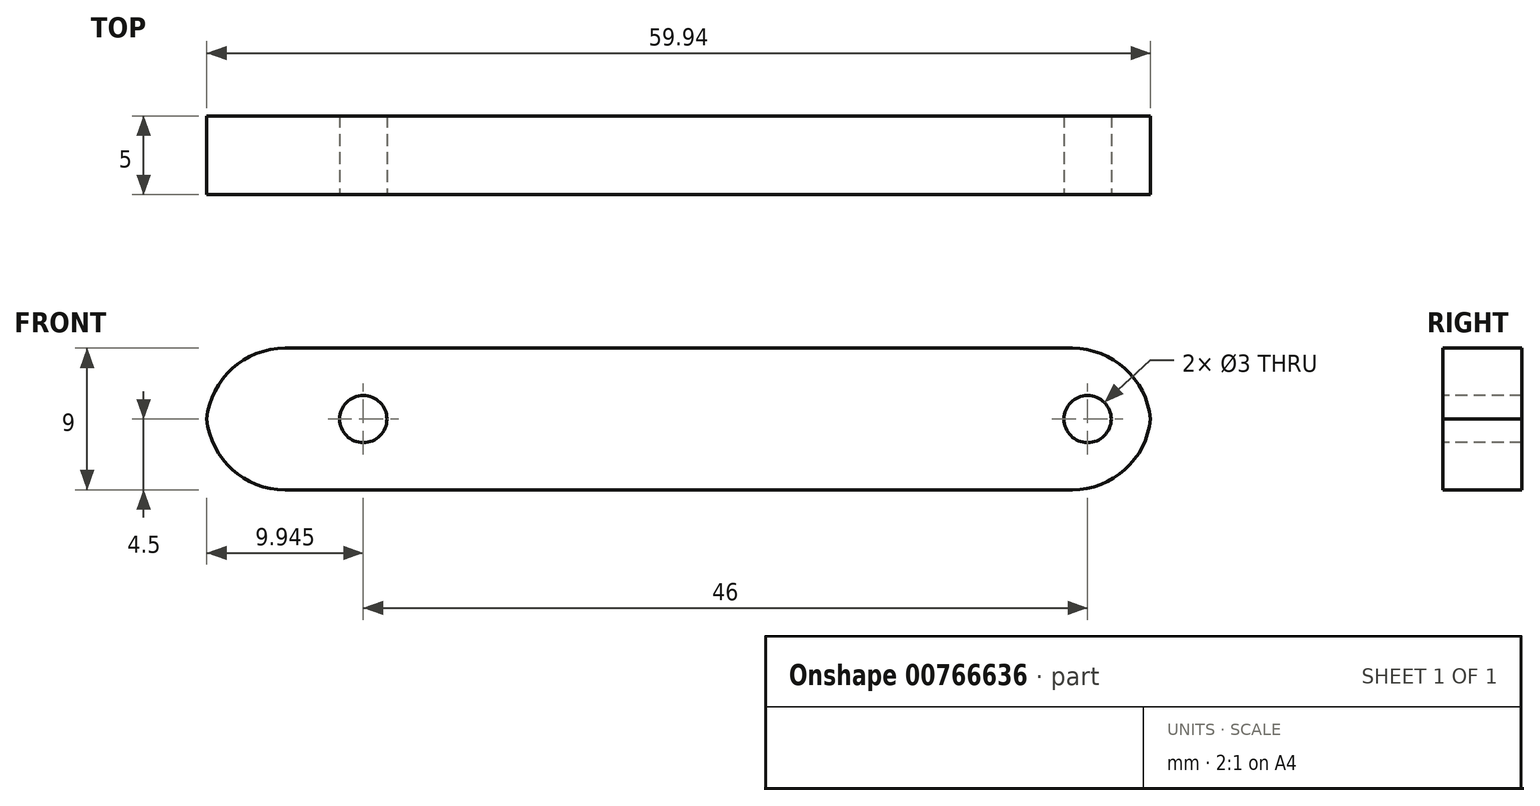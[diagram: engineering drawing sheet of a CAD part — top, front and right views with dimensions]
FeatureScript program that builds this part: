
annotation { "Feature Type Name" : "Feature", "Feature Type Description" : "" }
export const myFeature = defineFeature(function(context is Context, id is Id, definition is map)
    precondition{}
    {
        {
            var Q0;
            Q0=qCreatedBy(makeId("Front.planeOp"),FACE);
            var sketch = newSketch(context, id + "F0", { "sketchPlane" : qUnion([Q0])});
            skLineSegment(sketch, "E0.bottom", {"start": v(-30, 4.5) * mm, "end": v(30, 4.5) * mm});
            skLineSegment(sketch, "E0.top", {"start": v(-30, -4.5) * mm, "end": v(30, -4.5) * mm});
            skLineSegment(sketch, "E0.left", {"start": v(-30, 4.5) * mm, "end": v(-30, -4.5) * mm});
            skLineSegment(sketch, "E0.right", {"start": v(30, 4.5) * mm, "end": v(30, -4.5) * mm});
            skPoint(sketch, "E0.middle", {"position": v(0, 0) * mm});
            skSolve(sketch);
        }
        {
            var Q0;
            Q0=makeQuery(id+"F0.imprint","IMPRINT",FACE,{"disambiguationData":[TD([[makeQuery(id+"F0.imprint","IMPRINT",EDGE,{"derivedFrom":sQuery(id+"F0.wireOp",EDGE,"E0.bottom")}),-1.0]])]});
            extrude(context, id + "F1", {"entities" : qUnion([Q0]), "depth" : 5 * mm, "offsetDistance" : 25 * mm});
        }
        {
            var Q0;
            Q0=makeQuery(id+"F1.opExtrude","SWEPT_EDGE",EDGE,{"disambiguationData":[OSD([sQuery(id+"F0.wireOp",EDGE,"E0.bottom"),sQuery(id+"F0.wireOp",EDGE,"E0.left")])]});
            var Q1;
            Q1=makeQuery(id+"F1.opExtrude","SWEPT_EDGE",EDGE,{"disambiguationData":[OSD([sQuery(id+"F0.wireOp",EDGE,"E0.top"),sQuery(id+"F0.wireOp",EDGE,"E0.left")])]});
            var Q2;
            Q2=makeQuery(id+"F1.opExtrude","SWEPT_EDGE",EDGE,{"disambiguationData":[OSD([sQuery(id+"F0.wireOp",EDGE,"E0.bottom"),sQuery(id+"F0.wireOp",EDGE,"E0.right")])]});
            var Q3;
            Q3=makeQuery(id+"F1.opExtrude","SWEPT_EDGE",EDGE,{"disambiguationData":[OSD([sQuery(id+"F0.wireOp",EDGE,"E0.top"),sQuery(id+"F0.wireOp",EDGE,"E0.right")])]});
            fillet(context, id + "F2", {"entities" : qUnion([Q0, Q1, Q2, Q3]), "radius" : 5 * mm, "tangentPropagation" : true, "allowEdgeOverflow" : false});
        }
        {
            var Q0;
            Q0=qCreatedBy(makeId("Front.planeOp"),FACE);
            var sketch = newSketch(context, id + "F3", { "sketchPlane" : qUnion([Q0])});
            skCircle(sketch, "E1", {"center": v(25.97, 0) * mm, "radius": 1.5 * mm});
            skCircle(sketch, "E2", {"center": v(-20.03, 0) * mm, "radius": 1.5 * mm});
            skSolve(sketch);
        }
        {
            var Q0;
            Q0 = qSketchRegion(id + "F3", true);
            extrude(context, id + "F4", {"entities" : qUnion([Q0]), "operationType" : NewBodyOperationType.REMOVE, "endBound" : BoundingType.SYMMETRIC, "oppositeDirection" : true, "depth" : 25 * mm, "offsetDistance" : 25 * mm});
        }
    });
